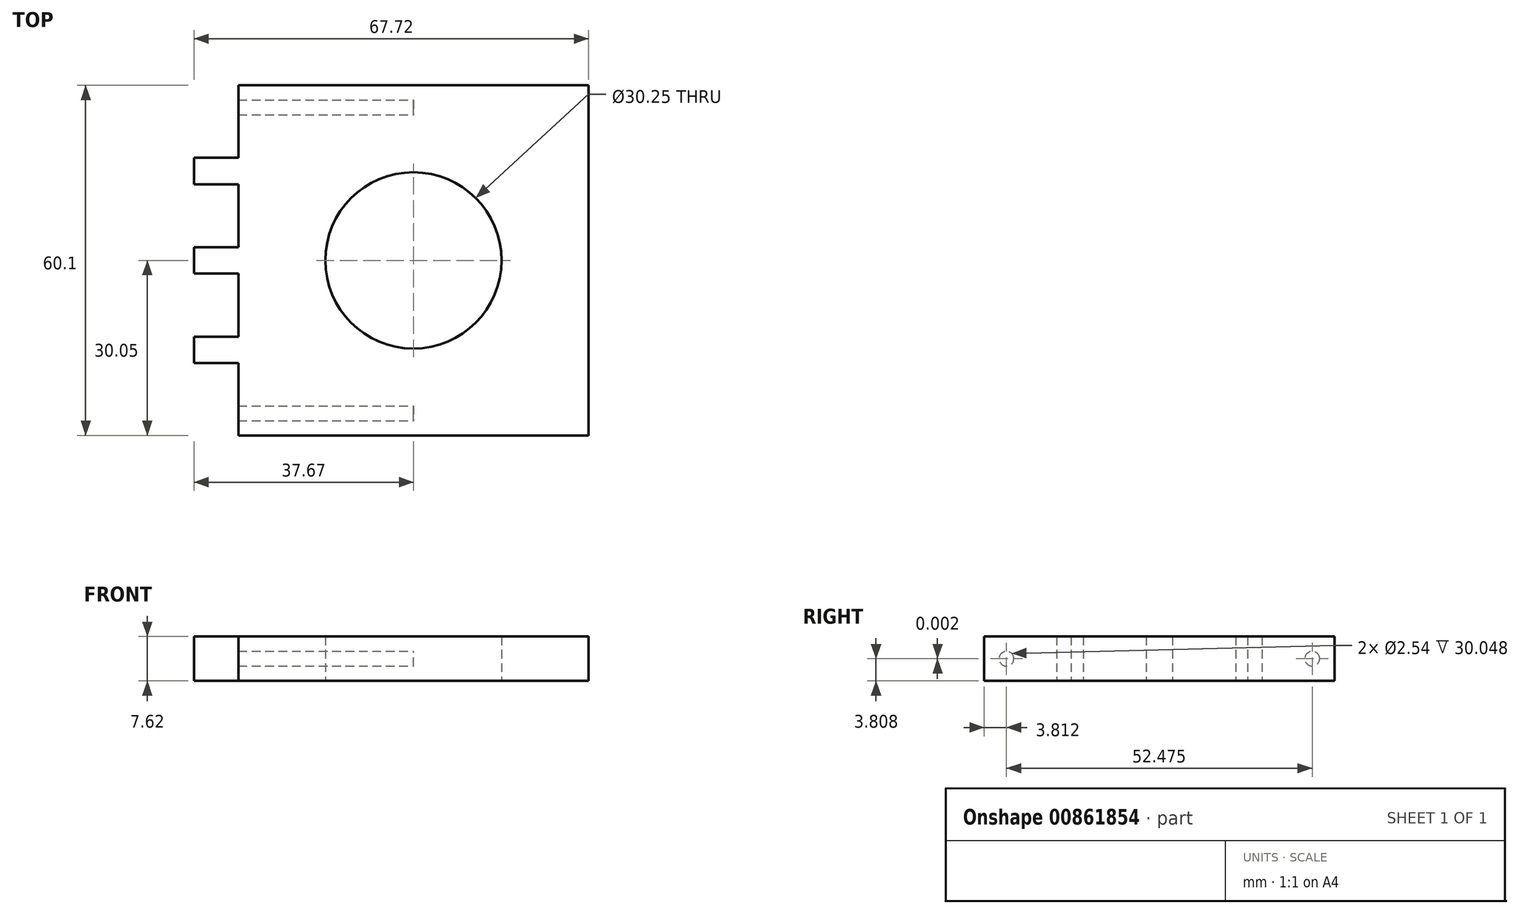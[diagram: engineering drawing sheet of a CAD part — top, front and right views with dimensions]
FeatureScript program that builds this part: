
annotation { "Feature Type Name" : "Feature", "Feature Type Description" : "" }
export const myFeature = defineFeature(function(context is Context, id is Id, definition is map)
    precondition{}
    {
        {
            var Q0;
            Q0=qCreatedBy(makeId("Top.planeOp"),FACE);
            var sketch = newSketch(context, id + "F0", { "sketchPlane" : qUnion([Q0])});
            skCircle(sketch, "E0", {"center": v(0, 0) * mm, "radius": 15.13 * mm});
            skLineSegment(sketch, "E1.bottom", {"start": v(-30.05, 30.05) * mm, "end": v(30.05, 30.05) * mm});
            skLineSegment(sketch, "E1.top", {"start": v(-30.05, -30.05) * mm, "end": v(30.05, -30.05) * mm});
            skLineSegment(sketch, "E1.left", {"start": v(-30.05, 30.05) * mm, "end": v(-30.05, -30.05) * mm});
            skLineSegment(sketch, "E1.right", {"start": v(30.05, 30.05) * mm, "end": v(30.05, -30.05) * mm});
            skLineSegment(sketch, "E2.bottom", {"start": v(-30.05, 2.26) * mm, "end": v(-37.67, 2.26) * mm});
            skLineSegment(sketch, "E2.top", {"start": v(-30.05, -2.26) * mm, "end": v(-37.67, -2.26) * mm});
            skLineSegment(sketch, "E2.left", {"start": v(-30.05, 2.26) * mm, "end": v(-30.05, -2.26) * mm});
            skLineSegment(sketch, "E2.right", {"start": v(-37.67, 2.26) * mm, "end": v(-37.67, -2.26) * mm});
            skLineSegment(sketch, "E3.bottom", {"start": v(-30.05, 17.6) * mm, "end": v(-37.67, 17.6) * mm});
            skLineSegment(sketch, "E3.top", {"start": v(-30.05, 13.08) * mm, "end": v(-37.67, 13.08) * mm});
            skLineSegment(sketch, "E3.left", {"start": v(-30.05, 17.6) * mm, "end": v(-30.05, 13.08) * mm});
            skLineSegment(sketch, "E3.right", {"start": v(-37.67, 17.6) * mm, "end": v(-37.67, 13.08) * mm});
            skLineSegment(sketch, "E4.bottom", {"start": v(-30.05, -13.08) * mm, "end": v(-37.67, -13.08) * mm});
            skLineSegment(sketch, "E4.top", {"start": v(-30.05, -17.6) * mm, "end": v(-37.67, -17.6) * mm});
            skLineSegment(sketch, "E4.left", {"start": v(-30.05, -13.08) * mm, "end": v(-30.05, -17.6) * mm});
            skLineSegment(sketch, "E4.right", {"start": v(-37.67, -13.08) * mm, "end": v(-37.67, -17.6) * mm});
            skSolve(sketch);
        }
        {
            var Q0;
            Q0=makeQuery(id+"F0.imprint","IMPRINT",FACE,{"disambiguationData":[TD([[makeQuery(id+"F0.imprint","IMPRINT",EDGE,{"derivedFrom":sQuery(id+"F0.wireOp",EDGE,"E0")}),-1.0]])]});
            var Q1;
            Q1=makeQuery(id+"F0.imprint","IMPRINT",FACE,{"disambiguationData":[TD([[makeQuery(id+"F0.imprint","IMPRINT",EDGE,{"derivedFrom":sQuery(id+"F0.wireOp",EDGE,"E3.bottom")}),1.0]])]});
            var Q2;
            Q2=makeQuery(id+"F0.imprint","IMPRINT",FACE,{"disambiguationData":[TD([[makeQuery(id+"F0.imprint","IMPRINT",EDGE,{"derivedFrom":sQuery(id+"F0.wireOp",EDGE,"E2.bottom")}),1.0]])]});
            var Q3;
            Q3=makeQuery(id+"F0.imprint","IMPRINT",FACE,{"disambiguationData":[TD([[makeQuery(id+"F0.imprint","IMPRINT",EDGE,{"derivedFrom":sQuery(id+"F0.wireOp",EDGE,"E4.bottom")}),1.0]])]});
            var Q4;
            Q4=sQuery(id+"F0.wireOp",EDGE,"E1.left");
            var Q5;
            Q5=sQuery(id+"F0.wireOp",EDGE,"E1.bottom");
            var Q6;
            Q6=sQuery(id+"F0.wireOp",EDGE,"E1.right");
            var Q7;
            Q7=sQuery(id+"F0.wireOp",EDGE,"E1.top");
            var Q8;
            Q8=sQuery(id+"F0.wireOp",EDGE,"E3.bottom");
            var Q9;
            Q9=sQuery(id+"F0.wireOp",EDGE,"E3.top");
            var Q10;
            Q10=sQuery(id+"F0.wireOp",EDGE,"E3.right");
            var Q11;
            Q11=sQuery(id+"F0.wireOp",EDGE,"E2.bottom");
            var Q12;
            Q12=sQuery(id+"F0.wireOp",EDGE,"E2.right");
            var Q13;
            Q13=sQuery(id+"F0.wireOp",EDGE,"E2.top");
            var Q14;
            Q14=sQuery(id+"F0.wireOp",EDGE,"E4.bottom");
            var Q15;
            Q15=sQuery(id+"F0.wireOp",EDGE,"E4.right");
            var Q16;
            Q16=sQuery(id+"F0.wireOp",EDGE,"E4.top");
            var Q17;
            Q17=sQuery(id+"F0.wireOp",EDGE,"E0");
            extrude(context, id + "F1", {"entities" : qUnion([Q0, Q1, Q2, Q3]), "surfaceOperationType" : NewSurfaceOperationType.ADD, "surfaceEntities" : qUnion([Q4, Q5, Q6, Q7, Q8, Q9, Q10, Q11, Q12, Q13, Q14, Q15, Q16, Q17]), "depth" : 7.62 * mm, "offsetDistance" : 25.4 * mm});
        }
        {
            var Q0;
            Q0=qCreatedBy(makeId("Right.planeOp"),FACE);
            var sketch = newSketch(context, id + "F2", { "sketchPlane" : qUnion([Q0])});
            skCircle(sketch, "E5", {"center": v(26.24, 3.8) * mm, "radius": 1.27 * mm});
            skSolve(sketch);
        }
        {
            var Q0;
            Q0 = qSketchRegion(id + "F2", true);
            var Q1;
            Q1=sQuery(id+"F2.wireOp",EDGE,"E5");
            extrude(context, id + "F3", {"entities" : qUnion([Q0]), "operationType" : NewBodyOperationType.REMOVE, "surfaceEntities" : qUnion([Q1]), "oppositeDirection" : true, "depth" : 32.97 * mm, "offsetDistance" : 25.4 * mm});
        }
        {
            var Q0;
            Q0=qCreatedBy(makeId("Right.planeOp"),FACE);
            var sketch = newSketch(context, id + "F4", { "sketchPlane" : qUnion([Q0])});
            skCircle(sketch, "E6", {"center": v(-26.24, 3.8) * mm, "radius": 1.27 * mm});
            skSolve(sketch);
        }
        {
            var Q0;
            Q0 = qSketchRegion(id + "F4", true);
            extrude(context, id + "F5", {"entities" : qUnion([Q0]), "operationType" : NewBodyOperationType.REMOVE, "oppositeDirection" : true, "depth" : 32.77 * mm, "offsetDistance" : 25.4 * mm});
        }
    });
